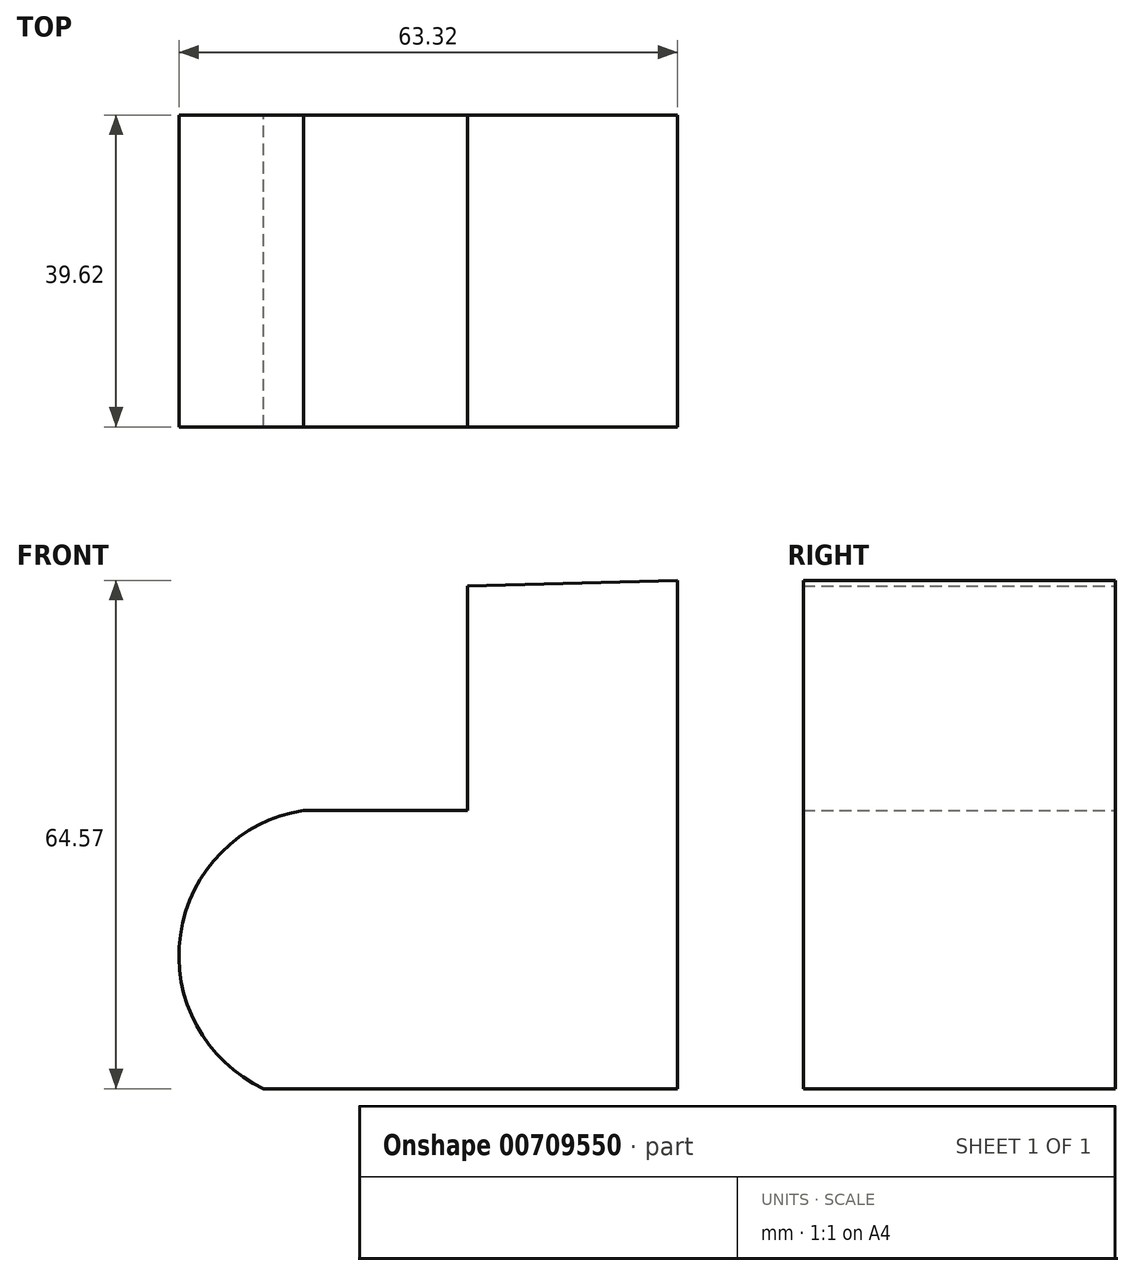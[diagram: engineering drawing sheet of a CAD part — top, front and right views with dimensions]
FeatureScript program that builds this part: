
annotation { "Feature Type Name" : "Feature", "Feature Type Description" : "" }
export const myFeature = defineFeature(function(context is Context, id is Id, definition is map)
    precondition{}
    {
        {
            var Q0;
            Q0=qCreatedBy(makeId("Front.planeOp"),FACE);
            var sketch = newSketch(context, id + "F0", { "sketchPlane" : qUnion([Q0])});
            skLineSegment(sketch, "E0", {"start": v(47.49, 64.57) * mm, "end": v(47.49, 0) * mm});
            skLineSegment(sketch, "E1", {"start": v(47.49, 0) * mm, "end": v(-5.07, 0) * mm});
            skArc(sketch, "E2", {"start": v(0, 35.35) * mm, "mid": v(-15.64, 19.55) * mm, "end": v(-5.07, 0) * mm});
            skLineSegment(sketch, "E3", {"start": v(0, 35.35) * mm, "end": v(20.86, 35.35) * mm});
            skLineSegment(sketch, "E4", {"start": v(20.86, 35.35) * mm, "end": v(20.86, 63.87) * mm});
            skLineSegment(sketch, "E5", {"start": v(20.86, 63.87) * mm, "end": v(47.49, 64.57) * mm});
            skSolve(sketch);
        }
        {
            var Q0;
            Q0 = qSketchRegion(id + "F0", true);
            extrude(context, id + "F1", {"entities" : qUnion([Q0]), "depth" : 39.62 * mm, "offsetDistance" : 25.4 * mm});
        }
    });
